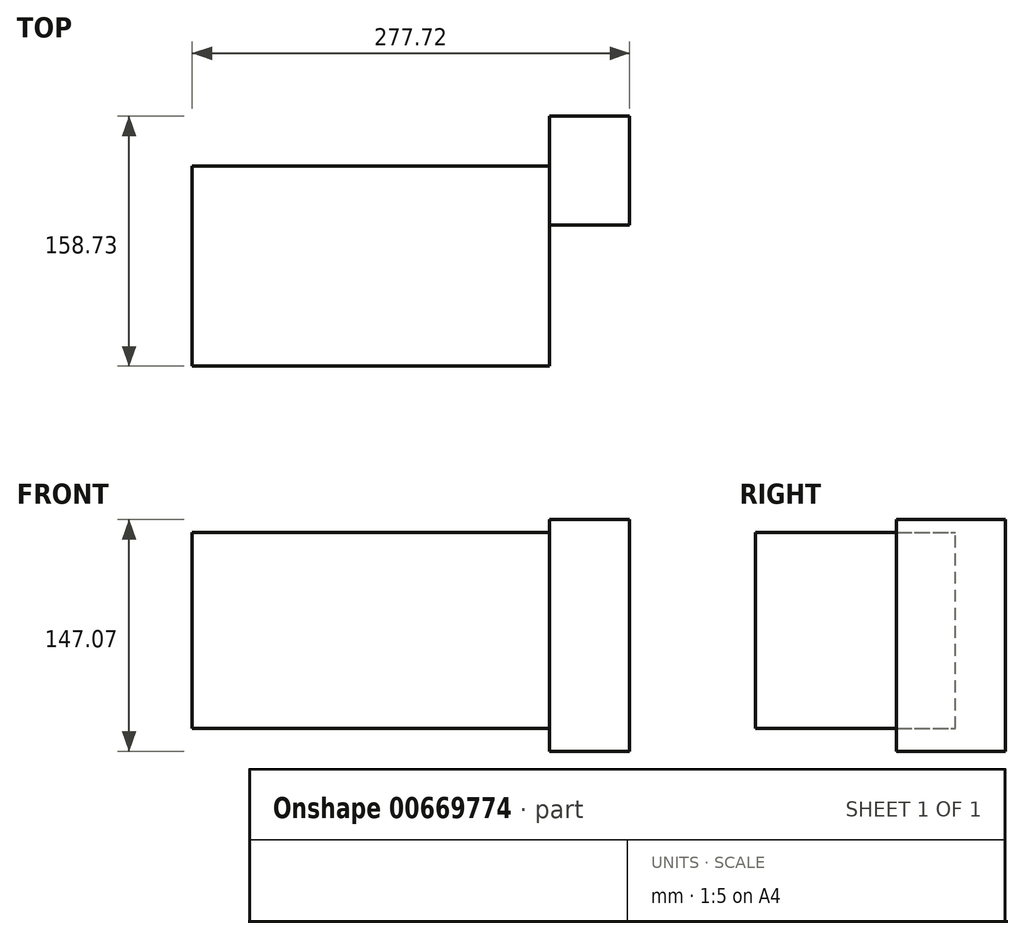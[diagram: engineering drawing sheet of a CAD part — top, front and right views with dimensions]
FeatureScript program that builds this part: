
annotation { "Feature Type Name" : "Feature", "Feature Type Description" : "" }
export const myFeature = defineFeature(function(context is Context, id is Id, definition is map)
    precondition{}
    {
        {
            var Q0;
            Q0=qCreatedBy(makeId("Front.planeOp"),FACE);
            var sketch = newSketch(context, id + "F0", { "sketchPlane" : qUnion([Q0])});
            skLineSegment(sketch, "E0.bottom", {"start": v(-113.46, -62.2) * mm, "end": v(113.46, -62.2) * mm});
            skLineSegment(sketch, "E0.top", {"start": v(-113.46, 62.2) * mm, "end": v(113.46, 62.2) * mm});
            skLineSegment(sketch, "E0.left", {"start": v(-113.46, -62.2) * mm, "end": v(-113.46, 62.2) * mm});
            skLineSegment(sketch, "E0.right", {"start": v(113.46, -62.2) * mm, "end": v(113.46, 62.2) * mm});
            skPoint(sketch, "E0.middle", {"position": v(0, 0) * mm});
            skSolve(sketch);
        }
        {
            var Q0;
            Q0 = qSketchRegion(id + "F0", true);
            extrude(context, id + "F1", {"entities" : qUnion([Q0]), "depth" : 127 * mm, "offsetDistance" : 25.4 * mm});
        }
        {
            var Q0;
            Q0=makeQuery(id+"F1.opExtrude","SWEPT_FACE",FACE,{"disambiguationData":[OSD([sQuery(id+"F0.wireOp",EDGE,"E0.right")])]});
            var sketch = newSketch(context, id + "F2", { "sketchPlane" : qUnion([Q0])});
            skLineSegment(sketch, "E1.bottom", {"start": v(-37.34, 70.37) * mm, "end": v(31.73, 70.37) * mm});
            skLineSegment(sketch, "E1.top", {"start": v(-37.34, -76.7) * mm, "end": v(31.73, -76.7) * mm});
            skLineSegment(sketch, "E1.left", {"start": v(-37.34, 70.37) * mm, "end": v(-37.34, -76.7) * mm});
            skLineSegment(sketch, "E1.right", {"start": v(31.73, 70.37) * mm, "end": v(31.73, -76.7) * mm});
            skSolve(sketch);
        }
        {
            var Q0;
            Q0 = qSketchRegion(id + "F2", true);
            extrude(context, id + "F3", {"entities" : qUnion([Q0]), "operationType" : NewBodyOperationType.ADD, "depth" : 50.8 * mm, "offsetDistance" : 25.4 * mm});
        }
    });
